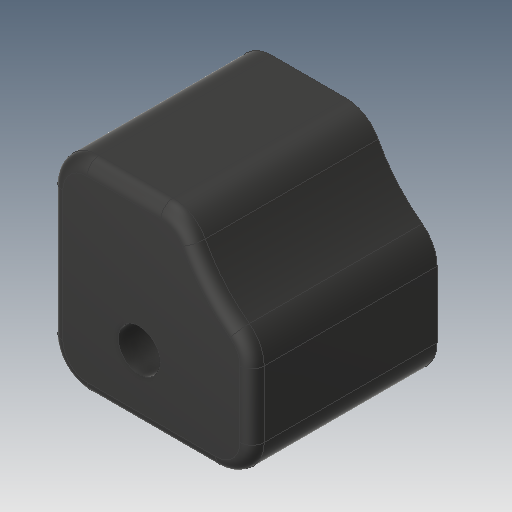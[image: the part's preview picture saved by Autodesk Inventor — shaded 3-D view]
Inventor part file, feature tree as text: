
AUTODESK INVENTOR PART (.ipt)
format: ipt  version: 2017 (Build 210142000, 142)  size: 196,096 bytes
history: native  units: in
note: dims shown in document units (in); Inventor stores cm internally (conversion verified against a paired STEP export)
features: sketch x3, extrude x3, plane x1, fillet x1, projected_geometry x1
ambient origin geometry x8: Origin, YZ Plane, XZ Plane, XY Plane, X Axis, Y Axis, Z Axis, Center Point
bodies: Solid1 (feature_tree)
feature tree (9):
  sketch  "Sketch1"  dims[d0=0.1181in d1=0.1181in d2=1.0in d3=0.0in]
  plane  "Work Plane1"
  extrude  "Extrusion1"  Depth=0.1181in TaperAngle=0.0deg
  extrude  "Extrusion2"  Depth=0.0787in TaperAngle=0.0deg
  extrude  "Extrusion3"  Depth=0.0394in
  fillet  "Fillet1"  Radius=0.0787in
  sketch  "Sketch2"  dims[d4=0.0197in d5=0.0787in d6=0.0in]
  projected_geometry  "Projected Loop1"
  sketch  "Sketch3"  dims[d7=0.2085in d8=0.315in d9=0.0787in d10=0.0in d11=0.0394in]
